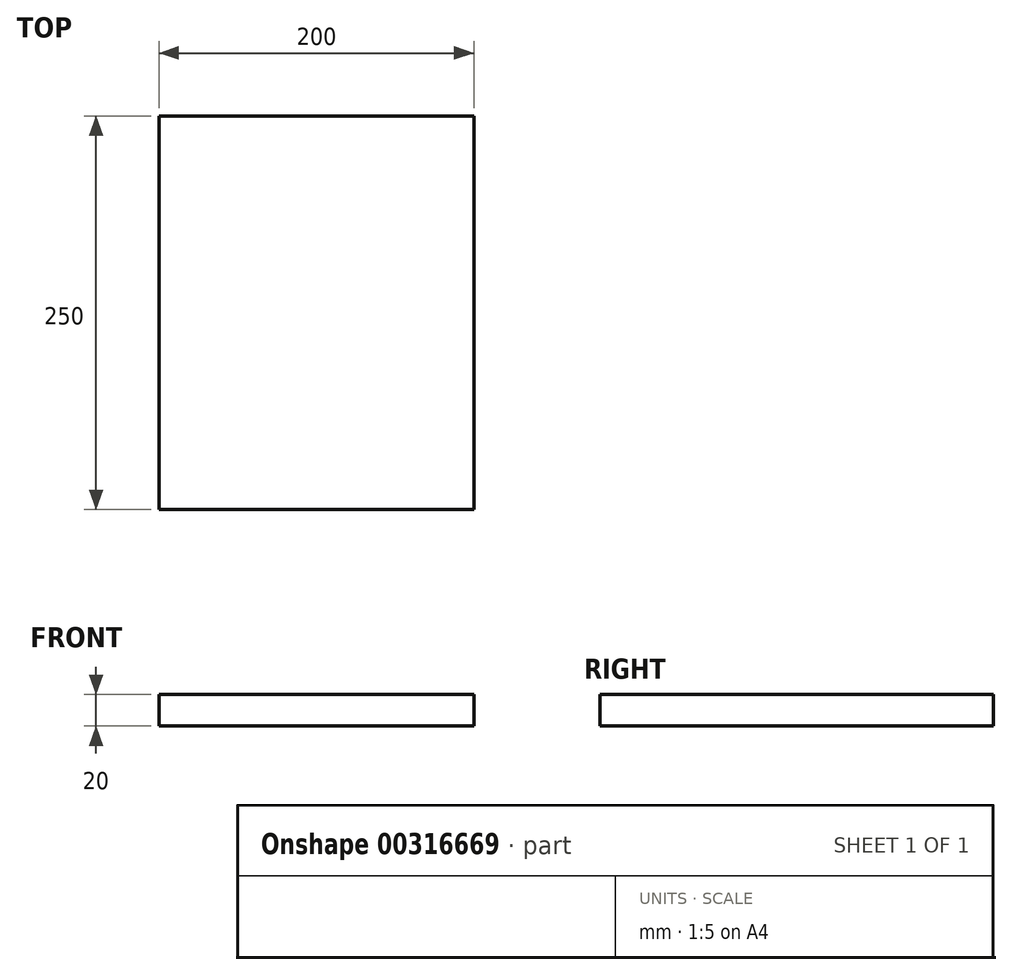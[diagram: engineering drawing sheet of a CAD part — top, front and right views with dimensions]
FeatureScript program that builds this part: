
annotation { "Feature Type Name" : "Feature", "Feature Type Description" : "" }
export const myFeature = defineFeature(function(context is Context, id is Id, definition is map)
    precondition{}
    {
        {
            var Q0;
            Q0=qCreatedBy(makeId("Top.planeOp"),FACE);
            var sketch = newSketch(context, id + "F0", { "sketchPlane" : qUnion([Q0])});
            skLineSegment(sketch, "E0.bottom", {"start": v(0, 0) * mm, "end": v(200, 0) * mm});
            skLineSegment(sketch, "E0.top", {"start": v(0, 250) * mm, "end": v(200, 250) * mm});
            skLineSegment(sketch, "E0.left", {"start": v(0, 0) * mm, "end": v(0, 250) * mm});
            skLineSegment(sketch, "E0.right", {"start": v(200, 0) * mm, "end": v(200, 250) * mm});
            skSolve(sketch);
        }
        {
            var Q0;
            Q0 = qSketchRegion(id + "F0", true);
            extrude(context, id + "F1", {"entities" : qUnion([Q0]), "depth" : 20 * mm});
        }
    });
